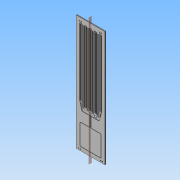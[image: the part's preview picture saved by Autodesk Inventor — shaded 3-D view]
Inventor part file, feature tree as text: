
AUTODESK INVENTOR PART (.ipt)
format: ipt  version: 2013 (Build 170138000, 138)  size: 446,464 bytes
history: native  units: in
note: dims shown in document units (in); Inventor stores cm internally (conversion verified against a paired STEP export)
features: other x15, extrude x5, hole x1, plane x1
ambient origin geometry x8: Origin, YZ Plane, XZ Plane, XY Plane, X Axis, Y Axis, Z Axis, Center Point
bodies: Solid1 (feature_tree)
feature tree (22):
  other  "Blocks"
  extrude  "Stock Extrusion"  Depth=23.8125in
  extrude  "Main rope pocket"  Depth=96.0in
  other  "Side profile reference"
  hole  "Hole1"  [1 undecoded]
  plane  "Work Plane1"
  extrude  "Through Panel Extrusion5"  Depth=58.0in
  other  "Exclaim Point"
  other  "Removal extra wood"
  other  "SignCenter"
  extrude  "Point pocket"  Depth=1.0in
  extrude  "Extrusion8"  Depth=2.9062in
  other  "Stock"
  other  "LEDPocket"
  other  "TwoLineColumn"
  other  "TwoLineColumnEnd"
  other  "15mm Neon profile"
  other  "U Bolt hole and bore"
  other  "U-Bolt holes"
  other  "WeatherProof panel"
  other  "15mm Neon profile:1"
  other  "15mm Neon profile:2"
note: 1 required parameter value undecoded (feature->parameter linkage not recoverable at this tier; creation-order binding heuristic only, values carry confidence <= 0.55)
